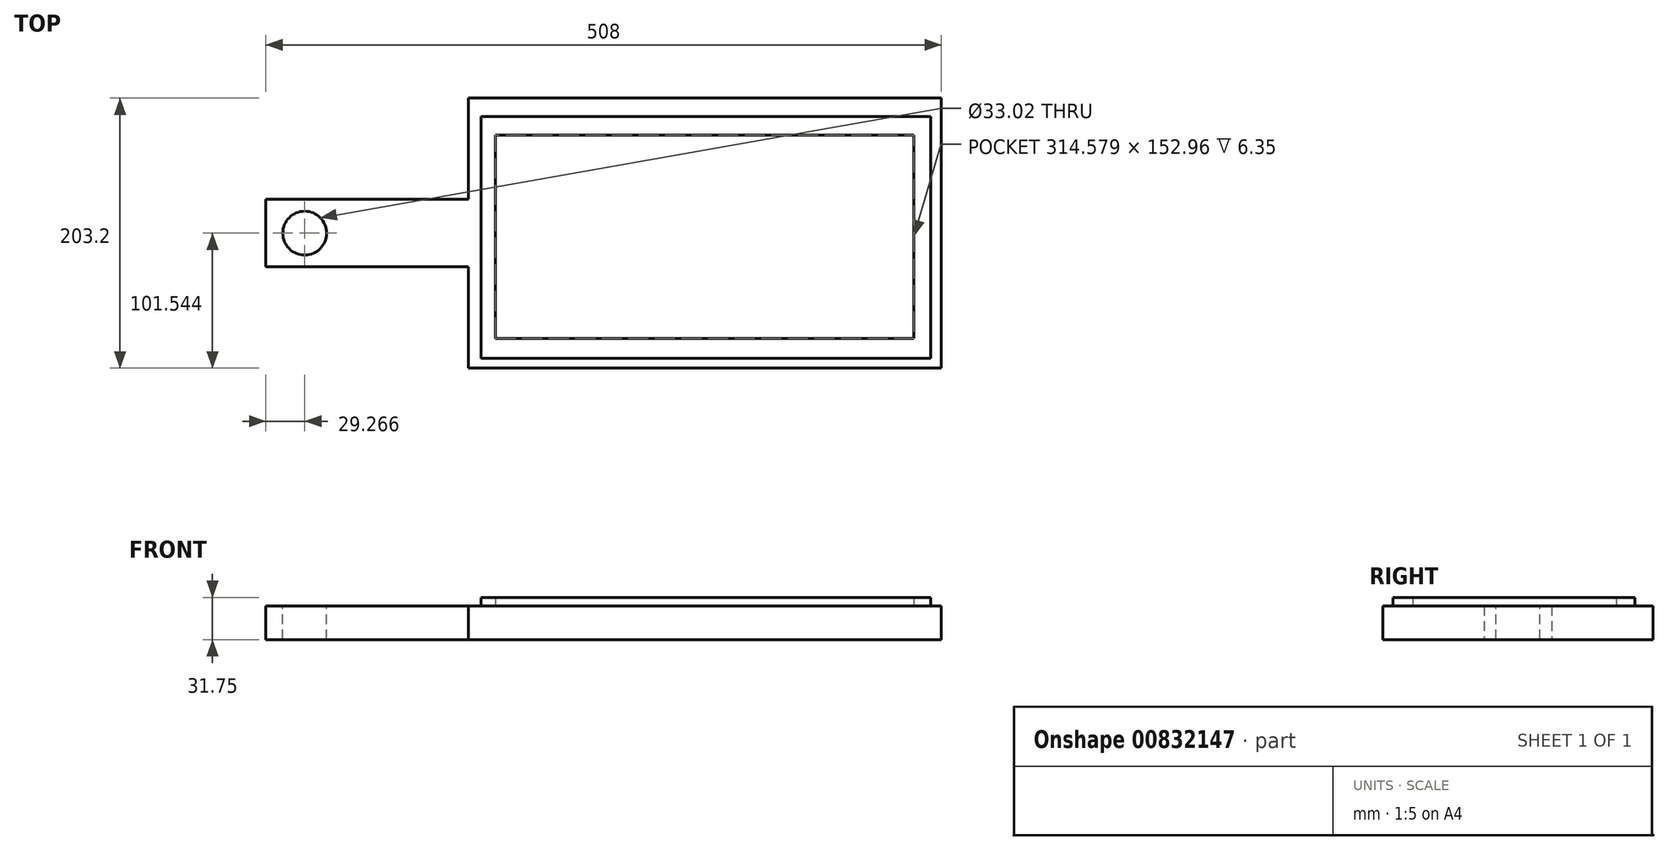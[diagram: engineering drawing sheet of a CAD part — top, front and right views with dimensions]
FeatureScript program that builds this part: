
annotation { "Feature Type Name" : "Feature", "Feature Type Description" : "" }
export const myFeature = defineFeature(function(context is Context, id is Id, definition is map)
    precondition{}
    {
        {
            var Q0;
            Q0=qCreatedBy(makeId("Top.planeOp"),FACE);
            var sketch = newSketch(context, id + "F0", { "sketchPlane" : qUnion([Q0])});
            skLineSegment(sketch, "E0.bottom", {"start": v(0, 0) * mm, "end": v(355.6, 0) * mm});
            skLineSegment(sketch, "E0.top", {"start": v(0, 203.2) * mm, "end": v(355.6, 203.2) * mm});
            skLineSegment(sketch, "E0.left", {"start": v(0, 0) * mm, "end": v(0, 203.2) * mm});
            skLineSegment(sketch, "E0.right", {"start": v(355.6, 0) * mm, "end": v(355.6, 203.2) * mm});
            skLineSegment(sketch, "E1.bottom", {"start": v(0, 127) * mm, "end": v(-152.4, 127) * mm});
            skLineSegment(sketch, "E1.top", {"start": v(0, 76.2) * mm, "end": v(-152.4, 76.2) * mm});
            skLineSegment(sketch, "E1.left", {"start": v(0, 127) * mm, "end": v(0, 76.2) * mm});
            skLineSegment(sketch, "E1.right", {"start": v(-152.4, 127) * mm, "end": v(-152.4, 76.2) * mm});
            skSolve(sketch);
        }
        {
            var Q0;
            {var subQ3=sQuery(id+"F0.wireOp",EDGE,"E0.bottom");Q0=makeQuery(id+"F0.imprint","IMPRINT",FACE,{"disambiguationData":[TD([[makeQuery(id+"F0.imprint","IMPRINT",EDGE,{"derivedFrom":subQ3}),1.0]])]});}
            var Q1;
            Q1=makeQuery(id+"F0.imprint","IMPRINT",FACE,{"disambiguationData":[TD([[makeQuery(id+"F0.imprint","IMPRINT",EDGE,{"derivedFrom":sQuery(id+"F0.wireOp",EDGE,"E1.bottom")}),1.0]])]});
            extrude(context, id + "F1", {"entities" : qUnion([Q0, Q1]), "depth" : 25.4 * mm, "offsetDistance" : 25.4 * mm});
        }
        {
            var Q0;
            Q0=makeQuery(id+"F1.opExtrude","CAP_FACE",FACE,{"disambiguationData":[OSD([sQuery(id+"F0.wireOp",EDGE,"E0.bottom"),sQuery(id+"F0.wireOp",EDGE,"E0.top"),sQuery(id+"F0.wireOp",EDGE,"E0.left"),sQuery(id+"F0.wireOp",EDGE,"E0.right"),sQuery(id+"F0.wireOp",EDGE,"E1.bottom"),sQuery(id+"F0.wireOp",EDGE,"E1.top"),sQuery(id+"F0.wireOp",EDGE,"E1.right")])],"isStart":false});
            var sketch = newSketch(context, id + "F2", { "sketchPlane" : qUnion([Q0])});
            skCircle(sketch, "E2", {"center": v(-123.13, 101.54) * mm, "radius": 16.51 * mm});
            skSolve(sketch);
        }
        {
            var Q0;
            Q0=makeQuery(id+"F2.imprint","IMPRINT",FACE,{"disambiguationData":[TD([[makeQuery(id+"F2.imprint","IMPRINT",EDGE,{"derivedFrom":sQuery(id+"F2.wireOp",EDGE,"E2")}),-1.0]])]});
            var sketch = newSketch(context, id + "F3", { "sketchPlane" : qUnion([Q0])});
            skLineSegment(sketch, "E3.bottom", {"start": v(9.44, 189.4) * mm, "end": v(347.55, 189.4) * mm});
            skLineSegment(sketch, "E3.top", {"start": v(9.44, 7.41) * mm, "end": v(347.55, 7.41) * mm});
            skLineSegment(sketch, "E3.left", {"start": v(9.44, 189.4) * mm, "end": v(9.44, 7.41) * mm});
            skLineSegment(sketch, "E3.right", {"start": v(347.55, 189.4) * mm, "end": v(347.55, 7.41) * mm});
            skLineSegment(sketch, "E4.bottom", {"start": v(20.42, 175.28) * mm, "end": v(335, 175.28) * mm});
            skLineSegment(sketch, "E4.top", {"start": v(20.42, 22.32) * mm, "end": v(335, 22.32) * mm});
            skLineSegment(sketch, "E4.left", {"start": v(20.42, 175.28) * mm, "end": v(20.42, 22.32) * mm});
            skLineSegment(sketch, "E4.right", {"start": v(335, 175.28) * mm, "end": v(335, 22.32) * mm});
            skSolve(sketch);
        }
        {
            var Q0;
            Q0 = qSketchRegion(id + "F3", true);
            extrude(context, id + "F4", {"entities" : qUnion([Q0]), "operationType" : NewBodyOperationType.ADD, "depth" : 6.35 * mm, "offsetDistance" : 25.4 * mm});
        }
        {
            var Q0;
            Q0=makeQuery(id+"F2.imprint","IMPRINT",FACE,{"disambiguationData":[TD([[makeQuery(id+"F2.imprint","IMPRINT",EDGE,{"derivedFrom":sQuery(id+"F2.wireOp",EDGE,"E2")}),1.0]])]});
            extrude(context, id + "F5", {"entities" : qUnion([Q0]), "operationType" : NewBodyOperationType.REMOVE, "oppositeDirection" : true, "depth" : 25.4 * mm, "offsetDistance" : 25.4 * mm});
        }
    });
